# Revit family: Atlas Basin 50cm PP
name_source: partatom
category: Plumbing Fixtures
units: mm (PartAtom-declared; Revit-internal decimal feet)

## family parameters
Always vertical = Yes
Cut with Voids When Loaded = No
Enable Cutting in Views = No
Maintain Annotation Orientation = No
OmniClass Number = 23.45.05.14.99
OmniClass Title = Other Sanitary Washing Plumbing Fixtures
Part Type = Normal
Room Calculation Point = No
Round Connector Dimension = Use Diameter
Shared = No
Work Plane-Based = No

## types (3) — shared parameters
Category = Wall Mounted Basin
Colour = White
Fixing Details = Basin Fixing Bolts not supplied, 8mm to 10mm bolts recommended
Manufacturer = Lecico SA
Material = Vitreous China
Model = Atlas Basin 50cm PP
URL = https://www.lecicosa.co.za
zero-valued in all types: Default Elevation

## per-type parameters (varying)
| type | Full Pedestal | Half Pedestal | No Pedestal | Product Code | Technical Dimensions |
| Atlas Basin 50cm PP - No Pedestal | No | No | Yes | ATLBASWHU0500UE | W500 x H175 x D410mm |
| Atlas Basin 50cm PP Full pedestal Combo | Yes | No | No | ATLDUOBAS0500BE | W500 x H795 x D410mm |
| Atlas Basin 50cm Madison Half Pedestal | No | Yes | No | ATLBASWHU0500UE, MADPEDSEM0000UE | W500 x H480 x D410mm |

## geometry (parser evidence)
native form markers: Sweep x12
no freeform markers — native parametric forms only
